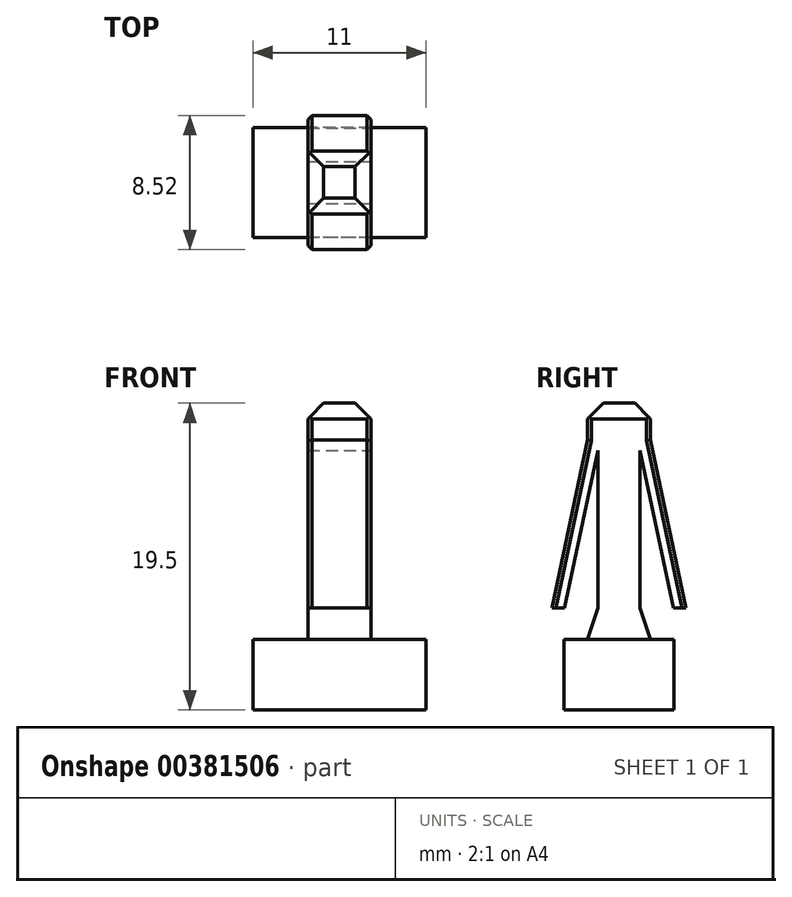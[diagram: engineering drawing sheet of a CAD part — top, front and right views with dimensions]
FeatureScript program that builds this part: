
annotation { "Feature Type Name" : "Feature", "Feature Type Description" : "" }
export const myFeature = defineFeature(function(context is Context, id is Id, definition is map)
    precondition{}
    {
        {
            var Q0;
            Q0=qCreatedBy(makeId("Top.planeOp"),FACE);
            var sketch = newSketch(context, id + "F0", { "sketchPlane" : qUnion([Q0])});
            skLineSegment(sketch, "E0.bottom", {"start": v(5.5, -3.5) * mm, "end": v(-5.5, -3.5) * mm});
            skLineSegment(sketch, "E0.top", {"start": v(5.5, 3.5) * mm, "end": v(-5.5, 3.5) * mm});
            skLineSegment(sketch, "E0.left", {"start": v(5.5, -3.5) * mm, "end": v(5.5, 3.5) * mm});
            skLineSegment(sketch, "E0.right", {"start": v(-5.5, -3.5) * mm, "end": v(-5.5, 3.5) * mm});
            skPoint(sketch, "E0.middle", {"position": v(0, 0) * mm});
            skSolve(sketch);
        }
        {
            var Q0;
            Q0 = qSketchRegion(id + "F0", true);
            extrude(context, id + "F1", {"entities" : qUnion([Q0]), "oppositeDirection" : true, "depth" : 4.5 * mm});
        }
        {
            var Q0;
            Q0=makeQuery(id+"F1.opExtrude","CAP_FACE",FACE,{"disambiguationData":[OSD([sQuery(id+"F0.wireOp",EDGE,"E0.bottom"),sQuery(id+"F0.wireOp",EDGE,"E0.top"),sQuery(id+"F0.wireOp",EDGE,"E0.left"),sQuery(id+"F0.wireOp",EDGE,"E0.right")])],"isStart":true});
            var sketch = newSketch(context, id + "F2", { "sketchPlane" : qUnion([Q0])});
            skLineSegment(sketch, "E1.bottom", {"start": v(2, -2) * mm, "end": v(-2, -2) * mm});
            skLineSegment(sketch, "E1.top", {"start": v(2, 2) * mm, "end": v(-2, 2) * mm});
            skLineSegment(sketch, "E1.left", {"start": v(2, -2) * mm, "end": v(2, 2) * mm});
            skLineSegment(sketch, "E1.right", {"start": v(-2, -2) * mm, "end": v(-2, 2) * mm});
            skPoint(sketch, "E1.middle", {"position": v(0, 0) * mm});
            skSolve(sketch);
        }
        {
            var Q0;
            Q0=makeQuery(id+"F2.imprint","IMPRINT",FACE,{"disambiguationData":[TD([[makeQuery(id+"F2.imprint","IMPRINT",EDGE,{"derivedFrom":sQuery(id+"F2.wireOp",EDGE,"E1.bottom")}),-1.0]])]});
            extrude(context, id + "F3", {"entities" : qUnion([Q0]), "operationType" : NewBodyOperationType.ADD, "depth" : 15 * mm});
        }
        {
            var Q0;
            Q0=makeQuery(id+"F3.opExtrude","SWEPT_FACE",FACE,{"disambiguationData":[OSD([sQuery(id+"F2.wireOp",EDGE,"E1.left")])]});
            var sketch = newSketch(context, id + "F4", { "sketchPlane" : qUnion([Q0])});
            skLineSegment(sketch, "E2", {"start": v(-1.5, 15) * mm, "end": v(-4.26, 2) * mm});
            skLineSegment(sketch, "E3", {"start": v(-4.26, 2) * mm, "end": v(-3.46, 2) * mm});
            skLineSegment(sketch, "E4", {"start": v(-3.46, 2) * mm, "end": v(-1.14, 12.94) * mm});
            skLineSegment(sketch, "E5", {"start": v(-1.14, 12.94) * mm, "end": v(-1.5, 15) * mm});
            skLineSegment(sketch, "E6.MirrorCS", {"start": v(4.26, 2) * mm, "end": v(3.46, 2) * mm});
            skLineSegment(sketch, "E7.MirrorCS", {"start": v(1.14, 12.94) * mm, "end": v(1.5, 15) * mm});
            skLineSegment(sketch, "E8.MirrorCS", {"start": v(1.5, 15) * mm, "end": v(4.26, 2) * mm});
            skLineSegment(sketch, "E9.MirrorCS", {"start": v(3.46, 2) * mm, "end": v(1.14, 12.94) * mm});
            skSolve(sketch);
        }
        {
            var Q0;
            Q0 = qSketchRegion(id + "F4", true);
            extrude(context, id + "F5", {"entities" : qUnion([Q0]), "operationType" : NewBodyOperationType.ADD, "oppositeDirection" : true, "depth" : 4 * mm});
        }
        {
            var Q0;
            Q0=makeQuery(id+"F5.boolean.opBoolean","MERGE",FACE,{"derivedFrom":[makeQuery(id+"F3.opExtrude","SWEPT_FACE",FACE,{"disambiguationData":[OSD([sQuery(id+"F2.wireOp",EDGE,"E1.left")])]}),makeQuery(id+"F5.opExtrude","CAP_FACE",FACE,{"disambiguationData":[OSD([sQuery(id+"F4.wireOp",EDGE,"E2"),sQuery(id+"F4.wireOp",EDGE,"E3"),sQuery(id+"F4.wireOp",EDGE,"E4"),sQuery(id+"F4.wireOp",EDGE,"E5")])],"isStart":true}),makeQuery(id+"F5.opExtrude","CAP_FACE",FACE,{"disambiguationData":[OSD([sQuery(id+"F4.wireOp",EDGE,"E6.MirrorCS"),sQuery(id+"F4.wireOp",EDGE,"E7.MirrorCS"),sQuery(id+"F4.wireOp",EDGE,"E8.MirrorCS"),sQuery(id+"F4.wireOp",EDGE,"E9.MirrorCS")])],"isStart":true})]});
            var sketch = newSketch(context, id + "F6", { "sketchPlane" : qUnion([Q0])});
            skLineSegment(sketch, "E10", {"start": v(-2, 8.88) * mm, "end": v(-1.34, 12) * mm});
            skLineSegment(sketch, "E11", {"start": v(-1.34, 12) * mm, "end": v(-1.34, 2) * mm});
            skLineSegment(sketch, "E12", {"start": v(-1.34, 2) * mm, "end": v(-2, 2) * mm});
            skLineSegment(sketch, "E13", {"start": v(-2, 2) * mm, "end": v(-2, 8.88) * mm});
            skLineSegment(sketch, "E14.MirrorCS", {"start": v(2, 8.88) * mm, "end": v(1.34, 12) * mm});
            skLineSegment(sketch, "E15.MirrorCS", {"start": v(1.34, 12) * mm, "end": v(1.34, 2) * mm});
            skLineSegment(sketch, "E16.MirrorCS", {"start": v(1.34, 2) * mm, "end": v(2, 2) * mm});
            skLineSegment(sketch, "E17.MirrorCS", {"start": v(2, 2) * mm, "end": v(2, 8.88) * mm});
            skLineSegment(sketch, "E18", {"start": v(-1.34, 2) * mm, "end": v(-2, 0) * mm});
            skLineSegment(sketch, "E19", {"start": v(-2, 0) * mm, "end": v(-2, 2) * mm});
            skLineSegment(sketch, "E20", {"start": v(1.34, 2) * mm, "end": v(2, 0) * mm});
            skLineSegment(sketch, "E21", {"start": v(2, 0) * mm, "end": v(2, 2) * mm});
            skSolve(sketch);
        }
        {
            var Q0;
            Q0 = qSketchRegion(id + "F6", true);
            extrude(context, id + "F7", {"entities" : qUnion([Q0]), "operationType" : NewBodyOperationType.REMOVE, "oppositeDirection" : true, "depth" : 25 * mm});
        }
        {
            var Q0;
            Q0=makeQuery(id+"F3.opExtrude","CAP_EDGE",EDGE,{"disambiguationData":[OSD([sQuery(id+"F2.wireOp",EDGE,"E1.right")])],"isStart":false});
            var Q1;
            Q1=makeQuery(id+"F3.opExtrude","CAP_EDGE",EDGE,{"disambiguationData":[OSD([sQuery(id+"F2.wireOp",EDGE,"E1.top")])],"isStart":false});
            var Q2;
            Q2=makeQuery(id+"F3.opExtrude","CAP_EDGE",EDGE,{"disambiguationData":[OSD([sQuery(id+"F2.wireOp",EDGE,"E1.left")])],"isStart":false});
            var Q3;
            Q3=makeQuery(id+"F3.opExtrude","CAP_EDGE",EDGE,{"disambiguationData":[OSD([sQuery(id+"F2.wireOp",EDGE,"E1.bottom")])],"isStart":false});
            chamfer(context, id + "F8", {"entities" : qUnion([Q0, Q1, Q2, Q3]), "width" : 1 * mm, "tangentPropagation" : true});
        }
        {
            var Q0;
            {var subQ0=sQuery(id+"F4.wireOp",EDGE,"E2");var subQ1=sQuery(id+"F2.wireOp",EDGE,"E1.left");var subQ2=sQuery(id+"F2.wireOp",EDGE,"E1.bottom");Q0=makeQuery(id+"F5.boolean.opBoolean","SPLIT",EDGE,{"disambiguationData":[TD([makeQuery(id+"F5.opExtrude","SWEPT_FACE",FACE,{"disambiguationData":[OSD([subQ0])]})])],"derivedFrom":makeQuery(id+"F3.opExtrude","SWEPT_EDGE",EDGE,{"disambiguationData":[OSD([subQ2,subQ1])]})});}
            var Q1;
            Q1=makeQuery(id+"F5.opExtrude","CAP_EDGE",EDGE,{"disambiguationData":[OSD([sQuery(id+"F4.wireOp",EDGE,"E2")])],"isStart":true});
            var Q2;
            Q2=makeQuery(id+"F5.opExtrude","CAP_EDGE",EDGE,{"disambiguationData":[OSD([sQuery(id+"F4.wireOp",EDGE,"E2")])],"isStart":false});
            var Q3;
            {var subQ0=sQuery(id+"F4.wireOp",EDGE,"E2");var subQ1=sQuery(id+"F2.wireOp",EDGE,"E1.right");var subQ2=sQuery(id+"F2.wireOp",EDGE,"E1.bottom");Q3=makeQuery(id+"F5.boolean.opBoolean","SPLIT",EDGE,{"disambiguationData":[TD([makeQuery(id+"F5.opExtrude","SWEPT_FACE",FACE,{"disambiguationData":[OSD([subQ0])]})])],"derivedFrom":makeQuery(id+"F3.opExtrude","SWEPT_EDGE",EDGE,{"disambiguationData":[OSD([subQ2,subQ1])]})});}
            var Q4;
            Q4=makeQuery(id+"F5.opExtrude","CAP_EDGE",EDGE,{"disambiguationData":[OSD([sQuery(id+"F4.wireOp",EDGE,"E8.MirrorCS")])],"isStart":false});
            var Q5;
            {var subQ0=sQuery(id+"F2.wireOp",EDGE,"E1.right");var subQ1=sQuery(id+"F2.wireOp",EDGE,"E1.top");var subQ2=sQuery(id+"F4.wireOp",EDGE,"E8.MirrorCS");Q5=makeQuery(id+"F5.boolean.opBoolean","SPLIT",EDGE,{"disambiguationData":[TD([makeQuery(id+"F5.opExtrude","SWEPT_FACE",FACE,{"disambiguationData":[OSD([subQ2])]})])],"derivedFrom":makeQuery(id+"F3.opExtrude","SWEPT_EDGE",EDGE,{"disambiguationData":[OSD([subQ1,subQ0])]})});}
            var Q6;
            {var subQ0=sQuery(id+"F2.wireOp",EDGE,"E1.left");var subQ1=sQuery(id+"F4.wireOp",EDGE,"E8.MirrorCS");var subQ2=sQuery(id+"F2.wireOp",EDGE,"E1.top");Q6=makeQuery(id+"F5.boolean.opBoolean","SPLIT",EDGE,{"disambiguationData":[TD([makeQuery(id+"F5.opExtrude","SWEPT_FACE",FACE,{"disambiguationData":[OSD([subQ1])]})])],"derivedFrom":makeQuery(id+"F3.opExtrude","SWEPT_EDGE",EDGE,{"disambiguationData":[OSD([subQ2,subQ0])]})});}
            var Q7;
            Q7=makeQuery(id+"F5.opExtrude","CAP_EDGE",EDGE,{"disambiguationData":[OSD([sQuery(id+"F4.wireOp",EDGE,"E8.MirrorCS")])],"isStart":true});
            chamfer(context, id + "F9", {"entities" : qUnion([Q0, Q1, Q2, Q3, Q4, Q5, Q6, Q7]), "width" : .25 * mm, "tangentPropagation" : true});
        }
    });
